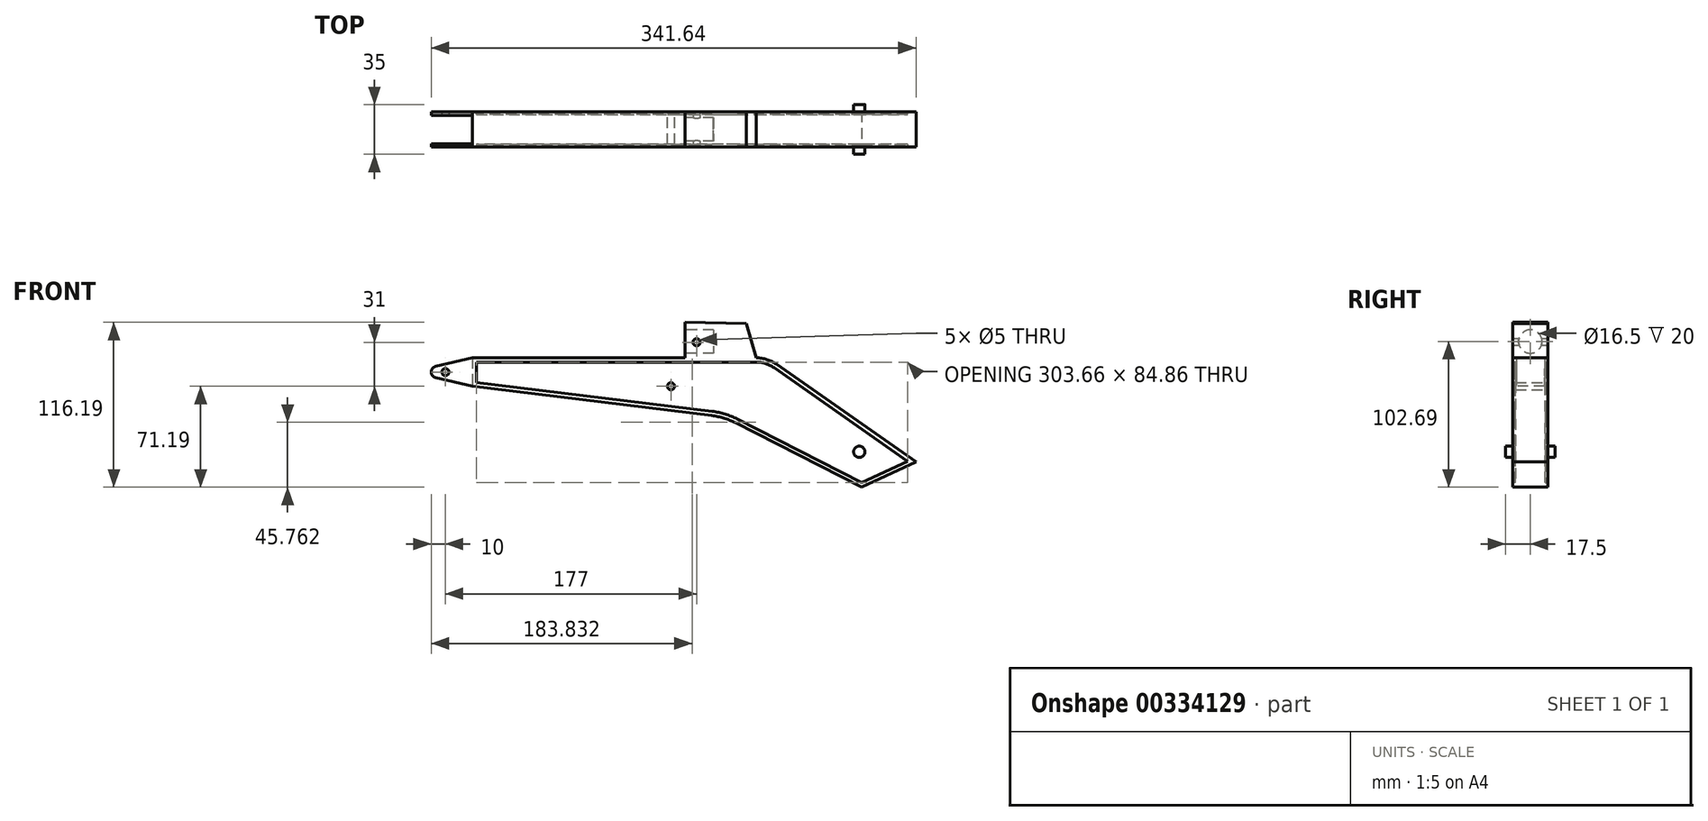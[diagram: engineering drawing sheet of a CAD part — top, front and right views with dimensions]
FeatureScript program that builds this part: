
annotation { "Feature Type Name" : "Feature", "Feature Type Description" : "" }
export const myFeature = defineFeature(function(context is Context, id is Id, definition is map)
    precondition{}
    {
        {
            var Q0;
            Q0=qCreatedBy(makeId("Front.planeOp"),FACE);
            var sketch = newSketch(context, id + "F0", { "sketchPlane" : qUnion([Q0])});
            skLineSegment(sketch, "E0", {"start": v(0, 20) * mm, "end": v(200, 20) * mm});
            skLineSegment(sketch, "E1", {"start": v(214.34, 15.48) * mm, "end": v(312.64, -53.35) * mm});
            skLineSegment(sketch, "E2", {"start": v(0, 20) * mm, "end": v(0, 0) * mm});
            skLineSegment(sketch, "E3", {"start": v(0, 0) * mm, "end": v(168.73, -20.72) * mm});
            skLineSegment(sketch, "E4", {"start": v(185.34, -25.8) * mm, "end": v(274.44, -71.2) * mm});
            skLineSegment(sketch, "E5", {"start": v(312.64, -53.35) * mm, "end": v(274.44, -71.2) * mm});
            skArc(sketch, "E6", {"start": v(-25.92, 13.9) * mm, "mid": v(-29, 10) * mm, "end": v(-25.92, 6.1) * mm});
            skPoint(sketch, "E6.centerSnap0", {"position": v(0, 10) * mm});
            skLineSegment(sketch, "E7", {"start": v(-25.92, 13.9) * mm, "end": v(0, 20) * mm});
            skLineSegment(sketch, "E8", {"start": v(-25.92, 6.1) * mm, "end": v(0, 0) * mm});
            skArc(sketch, "E9", {"start": v(214.34, 15.48) * mm, "mid": v(207.52, 18.84) * mm, "end": v(200, 20) * mm});
            skArc(sketch, "E10", {"start": v(185.34, -25.8) * mm, "mid": v(177.26, -22.53) * mm, "end": v(168.73, -20.72) * mm});
            skSolve(sketch);
        }
        {
            var Q0;
            Q0=makeQuery(id+"F0.imprint","IMPRINT",FACE,{"disambiguationData":[TD([[makeQuery(id+"F0.imprint","IMPRINT",EDGE,{"derivedFrom":sQuery(id+"F0.wireOp",EDGE,"E0")}),-1.0]])]});
            extrude(context, id + "F1", {"entities" : qUnion([Q0]), "oppositeDirection" : true, "depth" : 25 * mm});
        }
        {
            var Q0;
            Q0=makeQuery(id+"F0.imprint","IMPRINT",FACE,{"disambiguationData":[TD([[makeQuery(id+"F0.imprint","IMPRINT",EDGE,{"derivedFrom":sQuery(id+"F0.wireOp",EDGE,"E0")}),-1.0]])]});
            var sketch = newSketch(context, id + "F2", { "sketchPlane" : qUnion([Q0])});
            skLineSegment(sketch, "E11.0", {"start": v(186.7, -23.12) * mm, "end": v(274.5, -67.86) * mm});
            skArc(sketch, "E11.1", {"start": v(169.1, -17.74) * mm, "mid": v(178.14, -19.66) * mm, "end": v(186.7, -23.12) * mm});
            skLineSegment(sketch, "E11.2", {"start": v(274.5, -67.86) * mm, "end": v(306.66, -52.83) * mm});
            skLineSegment(sketch, "E11.3", {"start": v(3, 2.65) * mm, "end": v(169.1, -17.74) * mm});
            skLineSegment(sketch, "E11.4", {"start": v(306.66, -52.83) * mm, "end": v(212.62, 13.02) * mm});
            skArc(sketch, "E11.5", {"start": v(212.62, 13.02) * mm, "mid": v(206.62, 15.98) * mm, "end": v(200, 17) * mm});
            skLineSegment(sketch, "E11.6", {"start": v(200, 17) * mm, "end": v(3, 17) * mm});
            skLineSegment(sketch, "E11.7", {"start": v(3, 17) * mm, "end": v(3, 2.65) * mm});
            skSolve(sketch);
        }
        {
            var Q0;
            Q0 = qSketchRegion(id + "F2", true);
            extrude(context, id + "F3", {"entities" : qUnion([Q0]), "operationType" : NewBodyOperationType.REMOVE, "oppositeDirection" : true, "depth" : 2 * mm});
        }
        {
            var Q0;
            Q0=makeQuery(id+"F1.opExtrude","CAP_FACE",FACE,{"disambiguationData":[OSD([sQuery(id+"F0.wireOp",EDGE,"E0"),sQuery(id+"F0.wireOp",EDGE,"E1"),sQuery(id+"F0.wireOp",EDGE,"E2"),sQuery(id+"F0.wireOp",EDGE,"E3"),sQuery(id+"F0.wireOp",EDGE,"E4"),sQuery(id+"F0.wireOp",EDGE,"E5"),sQuery(id+"F0.wireOp",EDGE,"E9"),sQuery(id+"F0.wireOp",EDGE,"E10")])],"isStart":false});
            var sketch = newSketch(context, id + "F4", { "sketchPlane" : qUnion([Q0])});
            skLineSegment(sketch, "E12.0.0", {"start": v(-312.64, -53.35) * mm, "end": v(-274.44, -71.2) * mm});
            skLineSegment(sketch, "E12.0.1", {"start": v(-274.44, -71.2) * mm, "end": v(-185.34, -25.8) * mm});
            skArc(sketch, "E12.0.2", {"start": v(-185.34, -25.8) * mm, "mid": v(-177.26, -22.53) * mm, "end": v(-168.73, -20.72) * mm});
            skLineSegment(sketch, "E12.0.3", {"start": v(-168.73, -20.72) * mm, "end": v(0, 0) * mm});
            skLineSegment(sketch, "E12.0.4", {"start": v(0, 0) * mm, "end": v(0, 20) * mm});
            skLineSegment(sketch, "E12.0.5", {"start": v(0, 20) * mm, "end": v(-200, 20) * mm});
            skArc(sketch, "E12.0.6", {"start": v(-200, 20) * mm, "mid": v(-207.52, 18.84) * mm, "end": v(-214.34, 15.48) * mm});
            skLineSegment(sketch, "E12.0.7", {"start": v(-214.34, 15.48) * mm, "end": v(-312.64, -53.35) * mm});
            skLineSegment(sketch, "E13.0", {"start": v(-212.62, 13.02) * mm, "end": v(-306.66, -52.83) * mm});
            skArc(sketch, "E13.1", {"start": v(-200, 17) * mm, "mid": v(-206.62, 15.98) * mm, "end": v(-212.62, 13.02) * mm});
            skLineSegment(sketch, "E13.2", {"start": v(-306.66, -52.83) * mm, "end": v(-274.5, -67.86) * mm});
            skLineSegment(sketch, "E13.3", {"start": v(-3, 17) * mm, "end": v(-200, 17) * mm});
            skLineSegment(sketch, "E13.4", {"start": v(-274.5, -67.86) * mm, "end": v(-186.7, -23.12) * mm});
            skArc(sketch, "E13.5", {"start": v(-186.7, -23.12) * mm, "mid": v(-178.14, -19.66) * mm, "end": v(-169.1, -17.74) * mm});
            skLineSegment(sketch, "E13.6", {"start": v(-169.1, -17.74) * mm, "end": v(-3, 2.65) * mm});
            skLineSegment(sketch, "E13.7", {"start": v(-3, 2.65) * mm, "end": v(-3, 17) * mm});
            skSolve(sketch);
        }
        {
            var Q0;
            Q0=makeQuery(id+"F4.imprint","IMPRINT",FACE,{"disambiguationData":[TD([[makeQuery(id+"F4.imprint","IMPRINT",EDGE,{"derivedFrom":sQuery(id+"F4.wireOp",EDGE,"E13.0")}),1.0]])]});
            extrude(context, id + "F5", {"entities" : qUnion([Q0]), "operationType" : NewBodyOperationType.REMOVE, "oppositeDirection" : true, "depth" : 2 * mm});
        }
        {
            var Q0;
            Q0=makeQuery(id+"F0.imprint","IMPRINT",FACE,{"disambiguationData":[TD([[makeQuery(id+"F0.imprint","IMPRINT",EDGE,{"derivedFrom":sQuery(id+"F0.wireOp",EDGE,"E2")}),-1.0]])]});
            extrude(context, id + "F6", {"entities" : qUnion([Q0]), "operationType" : NewBodyOperationType.ADD, "oppositeDirection" : true, "depth" : 25 * mm});
        }
        {
            var Q0;
            Q0=qCreatedBy(makeId("Top.planeOp"),FACE);
            var sketch = newSketch(context, id + "F7", { "sketchPlane" : qUnion([Q0])});
            skLineSegment(sketch, "E14.bottom", {"start": v(0, 22.5) * mm, "end": v(-50, 22.5) * mm});
            skLineSegment(sketch, "E14.top", {"start": v(0, 2.5) * mm, "end": v(-50, 2.5) * mm});
            skLineSegment(sketch, "E14.left", {"start": v(0, 22.5) * mm, "end": v(0, 2.5) * mm});
            skLineSegment(sketch, "E14.right", {"start": v(-50, 22.5) * mm, "end": v(-50, 2.5) * mm});
            skSolve(sketch);
        }
        {
            var Q0;
            Q0 = qSketchRegion(id + "F7", true);
            extrude(context, id + "F8", {"entities" : qUnion([Q0]), "operationType" : NewBodyOperationType.REMOVE, "endBound" : BoundingType.THROUGH_ALL, "depth" : 25 * mm});
        }
        {
            var Q0;
            Q0=qCreatedBy(makeId("Front.planeOp"),FACE);
            var sketch = newSketch(context, id + "F9", { "sketchPlane" : qUnion([Q0])});
            skCircle(sketch, "E15", {"center": v(-19, 10) * mm, "radius": 2.5 * mm});
            skSolve(sketch);
        }
        {
            var Q0;
            Q0 = qSketchRegion(id + "F9", true);
            extrude(context, id + "F10", {"entities" : qUnion([Q0]), "operationType" : NewBodyOperationType.REMOVE, "endBound" : BoundingType.THROUGH_ALL, "oppositeDirection" : true, "depth" : 25 * mm});
        }
        {
            var Q0;
            Q0=qCreatedBy(makeId("Front.planeOp"),FACE);
            var sketch = newSketch(context, id + "F11", { "sketchPlane" : qUnion([Q0])});
            skLineSegment(sketch, "E16.0", {"start": v(150, 20) * mm, "end": v(200, 20) * mm});
            skLineSegment(sketch, "E17.0", {"start": v(200, 20) * mm, "end": v(200, 20) * mm});
            skLineSegment(sketch, "E18", {"start": v(150, 45) * mm, "end": v(150, 20) * mm});
            skPoint(sketch, "E19.orphan", {"position": v(0, 20) * mm});
            skPoint(sketch, "E20.orphan", {"position": v(214.34, 15.48) * mm});
            skLineSegment(sketch, "E21", {"start": v(150, 45) * mm, "end": v(193.15, 44.04) * mm});
            skLineSegment(sketch, "E22", {"start": v(193.15, 44.04) * mm, "end": v(200, 20) * mm});
            skSolve(sketch);
        }
        {
            var Q0;
            Q0 = qSketchRegion(id + "F11", true);
            extrude(context, id + "F12", {"entities" : qUnion([Q0]), "operationType" : NewBodyOperationType.ADD, "oppositeDirection" : true, "depth" : 25 * mm});
        }
        {
            var Q0;
            Q0=makeQuery(id+"F12.opExtrude","SWEPT_FACE",FACE,{"disambiguationData":[OSD([sQuery(id+"F11.wireOp",EDGE,"E18")])]});
            var sketch = newSketch(context, id + "F13", { "sketchPlane" : qUnion([Q0])});
            skSolve(sketch);
        }
        {
            var Q0;
            {var subQ0=sQuery(id+"F11.wireOp",EDGE,"E18");Q0=makeQuery(id+"F13.imprint","IMPRINT",FACE,{"disambiguationData":[TD([[makeQuery(id+"F13.imprint","IMPRINT",EDGE,{"derivedFrom":makeQuery(id+"F12.opExtrude","CAP_EDGE",EDGE,{"disambiguationData":[OSD([subQ0])],"isStart":true})}),-1.0]])]});}
            var sketch = newSketch(context, id + "F14", { "sketchPlane" : qUnion([Q0])});
            skCircle(sketch, "E23", {"center": v(-12.5, 31.5) * mm, "radius": 8.25 * mm});
            skSolve(sketch);
        }
        {
            var Q0;
            Q0 = qSketchRegion(id + "F14", true);
            extrude(context, id + "F15", {"entities" : qUnion([Q0]), "operationType" : NewBodyOperationType.REMOVE, "oppositeDirection" : true, "depth" : 20 * mm});
        }
        {
            var Q0;
            {var subQ0=sQuery(id+"F0.wireOp",EDGE,"E2");Q0=makeQuery(id+"F12.boolean.opBoolean","MERGE",FACE,{"derivedFrom":[makeQuery(id+"F6.boolean.opBoolean","MERGE",FACE,{"derivedFrom":[makeQuery(id+"F1.opExtrude","CAP_FACE",FACE,{"disambiguationData":[OSD([sQuery(id+"F0.wireOp",EDGE,"E0"),sQuery(id+"F0.wireOp",EDGE,"E1"),subQ0,sQuery(id+"F0.wireOp",EDGE,"E3"),sQuery(id+"F0.wireOp",EDGE,"E4"),sQuery(id+"F0.wireOp",EDGE,"E5"),sQuery(id+"F0.wireOp",EDGE,"E9"),sQuery(id+"F0.wireOp",EDGE,"E10")])],"isStart":true}),makeQuery(id+"F6.opExtrude","CAP_FACE",FACE,{"disambiguationData":[OSD([subQ0,sQuery(id+"F0.wireOp",EDGE,"E6"),sQuery(id+"F0.wireOp",EDGE,"E7"),sQuery(id+"F0.wireOp",EDGE,"E8")])],"isStart":true})]}),makeQuery(id+"F12.opExtrude","CAP_FACE",FACE,{"disambiguationData":[OSD([sQuery(id+"F11.wireOp",EDGE,"E16.0"),sQuery(id+"F11.wireOp",EDGE,"E17.0"),sQuery(id+"F11.wireOp",EDGE,"1uEiGn2F-jwPd-X9lV-y5Kc-w3AdLod2fVgB"),sQuery(id+"F11.wireOp",EDGE,"E18")])],"isStart":true})]});}
            var sketch = newSketch(context, id + "F16", { "sketchPlane" : qUnion([Q0])});
            skCircle(sketch, "E24", {"center": v(144.06, 31.64) * mm, "radius": 2.5 * mm});
            skSolve(sketch);
        }
        {
            var Q0;
            Q0 = qSketchRegion(id + "F16", true);
            extrude(context, id + "F17", {"entities" : qUnion([Q0]), "operationType" : NewBodyOperationType.REMOVE, "oppositeDirection" : true, "depth" : 25 * mm});
        }
        {
            var Q0;
            {var subQ0=sQuery(id+"F0.wireOp",EDGE,"E2");Q0=makeQuery(id+"F12.boolean.opBoolean","MERGE",FACE,{"derivedFrom":[makeQuery(id+"F6.boolean.opBoolean","MERGE",FACE,{"derivedFrom":[makeQuery(id+"F1.opExtrude","CAP_FACE",FACE,{"disambiguationData":[OSD([sQuery(id+"F0.wireOp",EDGE,"E0"),sQuery(id+"F0.wireOp",EDGE,"E1"),subQ0,sQuery(id+"F0.wireOp",EDGE,"E3"),sQuery(id+"F0.wireOp",EDGE,"E4"),sQuery(id+"F0.wireOp",EDGE,"E5"),sQuery(id+"F0.wireOp",EDGE,"E9"),sQuery(id+"F0.wireOp",EDGE,"E10")])],"isStart":true}),makeQuery(id+"F6.opExtrude","CAP_FACE",FACE,{"disambiguationData":[OSD([subQ0,sQuery(id+"F0.wireOp",EDGE,"E6"),sQuery(id+"F0.wireOp",EDGE,"E7"),sQuery(id+"F0.wireOp",EDGE,"E8")])],"isStart":true})]}),makeQuery(id+"F12.opExtrude","CAP_FACE",FACE,{"disambiguationData":[OSD([sQuery(id+"F11.wireOp",EDGE,"E16.0"),sQuery(id+"F11.wireOp",EDGE,"E18"),sQuery(id+"F11.wireOp",EDGE,"E21"),sQuery(id+"F11.wireOp",EDGE,"E22")])],"isStart":true})]});}
            var sketch = newSketch(context, id + "F18", { "sketchPlane" : qUnion([Q0])});
            skCircle(sketch, "E25", {"center": v(158, 31) * mm, "radius": 2.5 * mm});
            skSolve(sketch);
        }
        {
            var Q0;
            Q0 = qSketchRegion(id + "F18", true);
            extrude(context, id + "F19", {"entities" : qUnion([Q0]), "operationType" : NewBodyOperationType.REMOVE, "oppositeDirection" : true, "depth" : 25 * mm});
        }
        {
            var Q0;
            Q0=qCreatedBy(makeId("Front.planeOp"),FACE);
            cPlane(context, id + "F20", {"entities" : qUnion([Q0]), "cplaneType" : CPlaneType.OFFSET, "offset" : 12.5 * mm, "oppositeDirection" : true, "width" : 150 * mm, "height" : 150 * mm});
        }
        {
            var Q0;
            Q0=qCreatedBy(id+"F20.planeOp",FACE);
            var sketch = newSketch(context, id + "F21", { "sketchPlane" : qUnion([Q0])});
            skCircle(sketch, "E26", {"center": v(272.64, -46.2) * mm, "radius": 4 * mm});
            skSolve(sketch);
        }
        {
            var Q0;
            Q0 = qSketchRegion(id + "F21", true);
            extrude(context, id + "F22", {"entities" : qUnion([Q0]), "operationType" : NewBodyOperationType.ADD, "depth" : 35 * mm, "symmetric" : true});
        }
        {
            var Q0;
            Q0=qCreatedBy(id+"F20.planeOp",FACE);
            var sketch = newSketch(context, id + "F23", { "sketchPlane" : qUnion([Q0])});
            skCircle(sketch, "E27", {"center": v(140, 0) * mm, "radius": 2.5 * mm});
            skSolve(sketch);
        }
        {
            var Q0;
            Q0 = qSketchRegion(id + "F23", true);
            extrude(context, id + "F24", {"entities" : qUnion([Q0]), "operationType" : NewBodyOperationType.REMOVE, "depth" : 25 * mm, "symmetric" : true});
        }
    });
